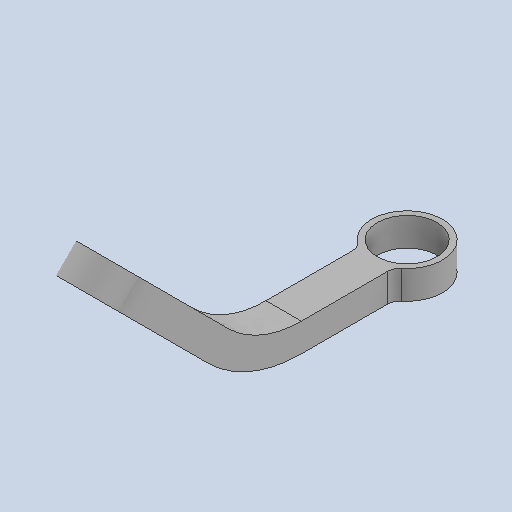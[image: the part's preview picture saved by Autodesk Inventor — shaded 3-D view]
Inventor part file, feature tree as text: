
AUTODESK INVENTOR PART (.ipt)
format: ipt  version: 2024 (Build 280153000, 153)  size: 320,512 bytes
history: native  units: mm
features: sketch x7, extrude x5, other x3, plane x2, sweep x1, mirror x1
ambient origin geometry x8: Origin, YZ Plane, XZ Plane, XY Plane, X Axis, Y Axis, Z Axis, Center Point
bodies: Solid1 (feature_tree)
feature tree (19):
  extrude  "Extrusion1"  Depth=12.0mm TaperAngle=0.0deg
  sweep  "Sweep2"
  plane  "Work Plane11"
  extrude  "Extrusion17"  TaperAngle=135.0deg  [1 undecoded]
  extrude  "Extrusion18"  TaperAngle=0.0deg  [1 undecoded]
  other  "Work Axis1"
  extrude  "Extrusion19"  Depth=12.0mm TaperAngle=0.0deg
  other  "Work Point2"
  extrude  "Extrusion21"  TaperAngle=0.0deg  [1 undecoded]
  mirror  "Mirror3"
  plane  "Work Plane13"
  sketch  "Sketch1"  dims[d0=30.0mm d1=12.0mm d2=0.0mm]
  sketch  "Sketch22"  dims[d109=5.0mm d110=50.0mm]
  sketch  "Sketch23"  dims[d111=70.0mm d112=135.0deg]
  sketch  "Sketch24"  dims[d113=50.0mm d114=0.0mm d115=0.0mm]
  sketch  "Sketch25"  dims[d116=-6.0mm d121=12.0mm d122=0.0mm]
  sketch  "Sketch26"  dims[d123=5.0mm d124=0.0mm d125=0.0mm]
  other  "Work Axis3"
  sketch  "Sketch28"  dims[d129=15.0mm d131=10.0mm d132=12.990381mm d133=25.2mm d134=10.0mm d135=0.0mm d136=22.0mm d137=12.0mm d141=16.2mm d142=5.0mm d143=0.0mm d150=12.5mm d74=0.5mm d75=0.872665mm d76=0.5mm d77=0.872665mm d98=0.0mm d99=0.0mm d100=0.0mm d101=0.0mm d102=0.872665mm d103=0.5mm d104=0.872665mm]
note: 3 required parameter values undecoded (feature->parameter linkage not recoverable at this tier; creation-order binding heuristic only, values carry confidence <= 0.55)
